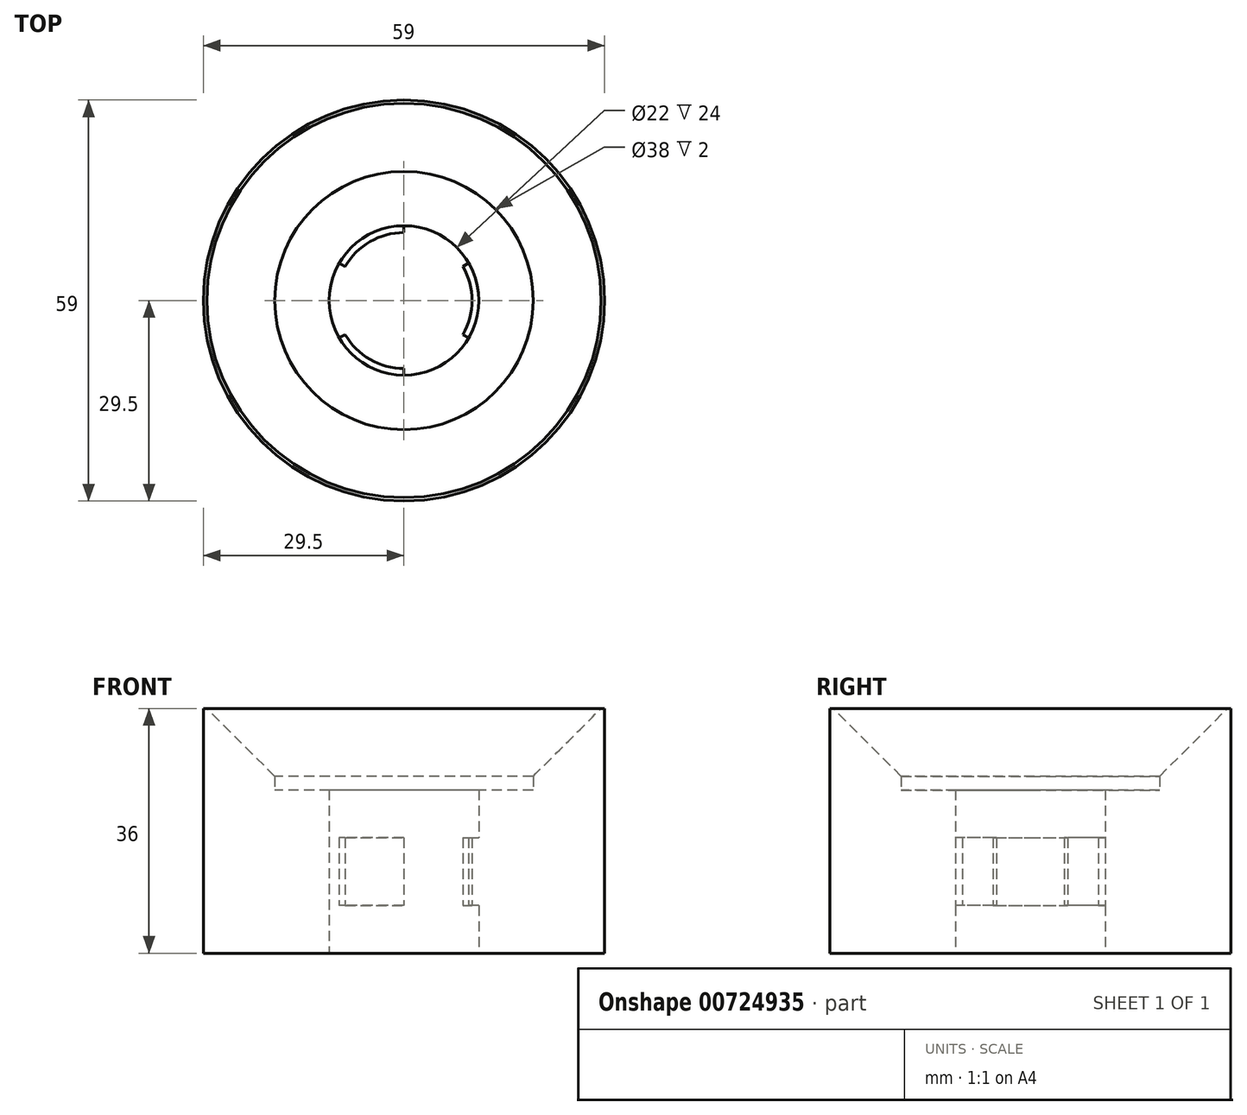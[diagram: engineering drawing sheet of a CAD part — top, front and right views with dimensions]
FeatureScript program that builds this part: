
annotation { "Feature Type Name" : "Feature", "Feature Type Description" : "" }
export const myFeature = defineFeature(function(context is Context, id is Id, definition is map)
    precondition{}
    {
        {
            var Q0;
            Q0=qCreatedBy(makeId("Top.planeOp"),FACE);
            var sketch = newSketch(context, id + "F0", { "sketchPlane" : qUnion([Q0])});
            skArc(sketch, "E0", {"start": v(0, 10) * mm, "mid": v(-5, 8.66) * mm, "end": v(-8.66, 5) * mm});
            skCircle(sketch, "E1", {"center": v(0, 0) * mm, "radius": 11 * mm});
            skCircle(sketch, "E2", {"center": v(0, 0) * mm, "radius": 19 * mm});
            skLineSegment(sketch, "E3", {"start": v(0, 10) * mm, "end": v(0, 11) * mm});
            skLineSegment(sketch, "E4.1.0", {"start": v(-8.66, 5) * mm, "end": v(-9.53, 5.5) * mm});
            skLineSegment(sketch, "E4.2.0", {"start": v(-8.66, -5) * mm, "end": v(-9.53, -5.5) * mm});
            skLineSegment(sketch, "E4.3.0", {"start": v(0, -10) * mm, "end": v(0, -11) * mm});
            skLineSegment(sketch, "E4.4.0", {"start": v(8.66, -5) * mm, "end": v(9.53, -5.5) * mm});
            skLineSegment(sketch, "E4.5.0", {"start": v(8.66, 5) * mm, "end": v(9.53, 5.5) * mm});
            skArc(sketch, "E5.trimOffspring", {"start": v(8.66, -5) * mm, "mid": v(10, 0) * mm, "end": v(8.66, 5) * mm});
            skArc(sketch, "E6.trimOffspring", {"start": v(-8.66, -5) * mm, "mid": v(-5, -8.66) * mm, "end": v(0, -10) * mm});
            skSolve(sketch);
        }
        {
            var Q0;
            Q0=makeQuery(id+"F0.imprint","IMPRINT",FACE,{"disambiguationData":[TD([[makeQuery(id+"F0.imprint","IMPRINT",EDGE,{"derivedFrom":sQuery(id+"F0.wireOp",EDGE,"E2")}),1.0]])]});
            var Q1;
            {var subQ0=sQuery(id+"F0.wireOp",EDGE,"E4.4.0");Q1=makeQuery(id+"F0.imprint","IMPRINT",FACE,{"disambiguationData":[TD([[makeQuery(id+"F0.imprint","IMPRINT",EDGE,{"derivedFrom":subQ0}),1.0]])]});}
            var Q2;
            Q2=makeQuery(id+"F0.imprint","IMPRINT",FACE,{"disambiguationData":[TD([[makeQuery(id+"F0.imprint","IMPRINT",EDGE,{"derivedFrom":sQuery(id+"F0.wireOp",EDGE,"E0")}),-1.0]])]});
            var Q3;
            {var subQ0=sQuery(id+"F0.wireOp",EDGE,"E4.2.0");Q3=makeQuery(id+"F0.imprint","IMPRINT",FACE,{"disambiguationData":[TD([[makeQuery(id+"F0.imprint","IMPRINT",EDGE,{"derivedFrom":subQ0}),1.0]])]});}
            extrude(context, id + "F1", {"entities" : qUnion([Q0, Q1, Q2, Q3]), "depth" : 24 * mm, "offsetDistance" : 25 * mm});
        }
        {
            var Q0;
            Q0=qCreatedBy(makeId("Top.planeOp"),FACE);
            var sketch = newSketch(context, id + "F2", { "sketchPlane" : qUnion([Q0])});
            skCircle(sketch, "E7", {"center": v(0, 0) * mm, "radius": 11 * mm});
            skSolve(sketch);
        }
        {
            var Q0;
            Q0 = qSketchRegion(id + "F2", true);
            extrude(context, id + "F3", {"entities" : qUnion([Q0]), "operationType" : NewBodyOperationType.REMOVE, "depth" : 7 * mm, "offsetDistance" : 25 * mm});
        }
        {
            var Q0;
            Q0=makeQuery(id+"F1.opExtrude","CAP_FACE",FACE,{"disambiguationData":[OSD([sQuery(id+"F0.wireOp",EDGE,"E0"),sQuery(id+"F0.wireOp",EDGE,"E1"),sQuery(id+"F0.wireOp",EDGE,"E2"),sQuery(id+"F0.wireOp",EDGE,"E3"),sQuery(id+"F0.wireOp",EDGE,"E4.1.0"),sQuery(id+"F0.wireOp",EDGE,"E4.2.0"),sQuery(id+"F0.wireOp",EDGE,"E4.3.0"),sQuery(id+"F0.wireOp",EDGE,"E4.4.0"),sQuery(id+"F0.wireOp",EDGE,"E4.5.0"),sQuery(id+"F0.wireOp",EDGE,"E5.trimOffspring"),sQuery(id+"F0.wireOp",EDGE,"E6.trimOffspring")])],"isStart":false});
            var sketch = newSketch(context, id + "F4", { "sketchPlane" : qUnion([Q0])});
            skCircle(sketch, "E8", {"center": v(0, 0) * mm, "radius": 11 * mm});
            skSolve(sketch);
        }
        {
            var Q0;
            Q0 = qSketchRegion(id + "F4", true);
            extrude(context, id + "F5", {"entities" : qUnion([Q0]), "operationType" : NewBodyOperationType.REMOVE, "oppositeDirection" : true, "depth" : 7 * mm, "offsetDistance" : 25 * mm});
        }
        {
            var Q0;
            Q0=qCreatedBy(makeId("Top.planeOp"),FACE);
            var sketch = newSketch(context, id + "F6", { "sketchPlane" : qUnion([Q0])});
            skCircle(sketch, "E9", {"center": v(0, 0) * mm, "radius": 29.5 * mm});
            skCircle(sketch, "E10", {"center": v(0, 0) * mm, "radius": 19 * mm});
            skSolve(sketch);
        }
        {
            var Q0;
            Q0=makeQuery(id+"F6.imprint","IMPRINT",FACE,{"disambiguationData":[TD([[makeQuery(id+"F6.imprint","IMPRINT",EDGE,{"derivedFrom":sQuery(id+"F6.wireOp",EDGE,"E9")}),1.0]])]});
            extrude(context, id + "F7", {"entities" : qUnion([Q0]), "operationType" : NewBodyOperationType.ADD, "depth" : 36 * mm, "offsetDistance" : 25 * mm});
        }
        {
            var Q0;
            Q0=makeQuery(id+"F7.opExtrude","CAP_EDGE",EDGE,{"disambiguationData":[OSD([sQuery(id+"F6.wireOp",EDGE,"E10")])],"isStart":false});
            chamfer(context, id + "F8", {"entities" : qUnion([Q0]), "width" : 10 * mm, "tangentPropagation" : true});
        }
    });
